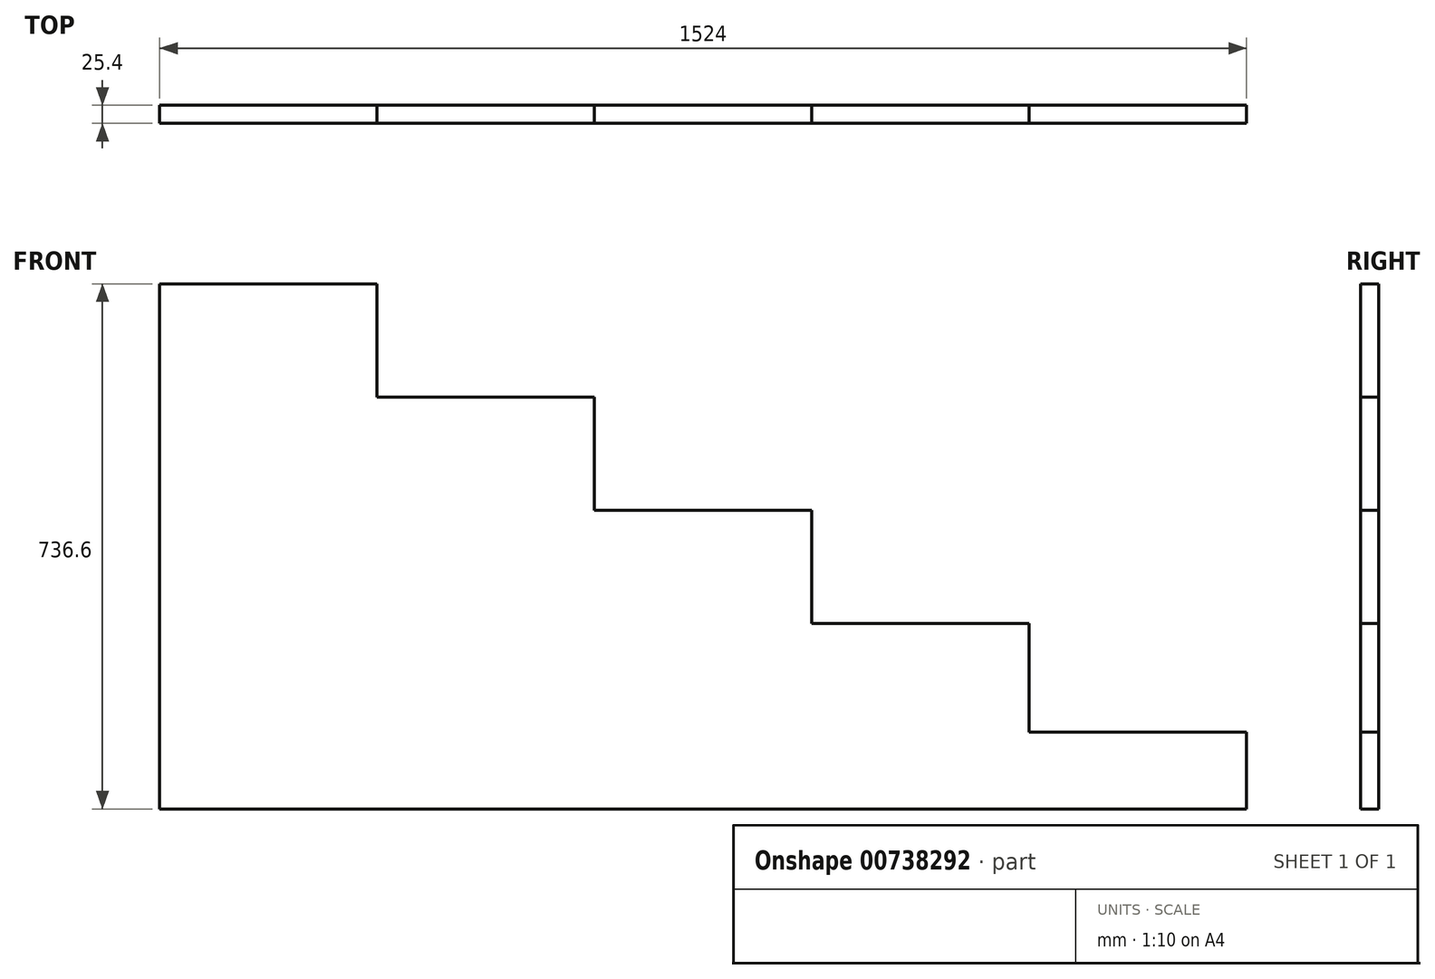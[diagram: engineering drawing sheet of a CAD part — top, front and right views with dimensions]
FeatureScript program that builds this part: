
annotation { "Feature Type Name" : "Feature", "Feature Type Description" : "" }
export const myFeature = defineFeature(function(context is Context, id is Id, definition is map)
    precondition{}
    {
        {
            var Q0;
            Q0=qCreatedBy(makeId("Front.planeOp"),FACE);
            var sketch = newSketch(context, id + "F0", { "sketchPlane" : qUnion([Q0])});
            skLineSegment(sketch, "E0", {"start": v(0, 0) * mm, "end": v(1524, 0) * mm});
            skLineSegment(sketch, "E1", {"start": v(0, 0) * mm, "end": v(0, 762) * mm});
            skLineSegment(sketch, "E2", {"start": v(1524, 0) * mm, "end": v(1524, 107.95) * mm});
            skLineSegment(sketch, "E3", {"start": v(1524, 107.95) * mm, "end": v(1219.2, 107.95) * mm});
            skLineSegment(sketch, "E4", {"start": v(1219.2, 107.95) * mm, "end": v(1219.2, 260.35) * mm});
            skLineSegment(sketch, "E5", {"start": v(1219.2, 260.35) * mm, "end": v(914.4, 260.35) * mm});
            skLineSegment(sketch, "E6", {"start": v(914.4, 260.35) * mm, "end": v(914.4, 419.1) * mm});
            skLineSegment(sketch, "E7", {"start": v(914.4, 419.1) * mm, "end": v(609.6, 419.1) * mm});
            skLineSegment(sketch, "E8", {"start": v(609.6, 419.1) * mm, "end": v(609.6, 577.85) * mm});
            skLineSegment(sketch, "E9", {"start": v(609.6, 577.85) * mm, "end": v(304.8, 577.85) * mm});
            skLineSegment(sketch, "E10", {"start": v(304.8, 577.85) * mm, "end": v(304.8, 736.6) * mm});
            skLineSegment(sketch, "E11", {"start": v(304.8, 736.6) * mm, "end": v(0, 736.6) * mm});
            skSolve(sketch);
        }
        {
            var Q0;
            {var subQ0=sQuery(id+"F0.wireOp",EDGE,"E0");Q0=makeQuery(id+"F0.imprint","IMPRINT",FACE,{"disambiguationData":[TD([[makeQuery(id+"F0.imprint","IMPRINT",EDGE,{"derivedFrom":subQ0}),1.0]])]});}
            extrude(context, id + "F1", {"entities" : qUnion([Q0]), "depth" : 25.4 * mm, "offsetDistance" : 25.4 * mm});
        }
    });
